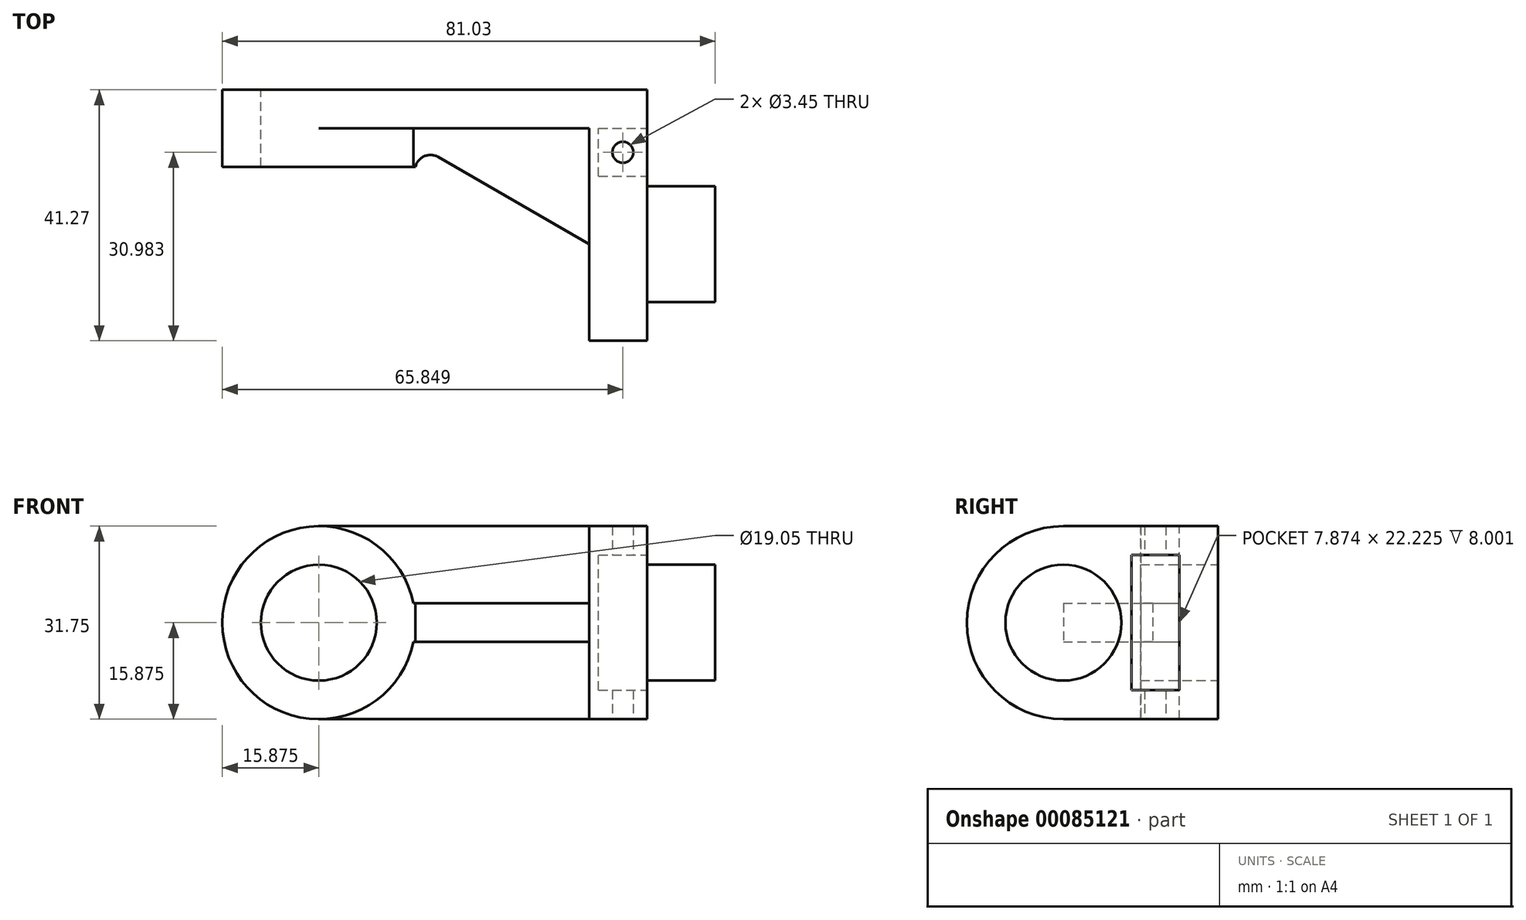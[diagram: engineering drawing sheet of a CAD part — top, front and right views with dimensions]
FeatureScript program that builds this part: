
annotation { "Feature Type Name" : "Feature", "Feature Type Description" : "" }
export const myFeature = defineFeature(function(context is Context, id is Id, definition is map)
    precondition{}
    {
        {
            var Q0;
            Q0=qCreatedBy(makeId("Front.planeOp"),FACE);
            var sketch = newSketch(context, id + "F0", { "sketchPlane" : qUnion([Q0])});
            skLineSegment(sketch, "E0.bottom", {"start": v(0, 0) * mm, "end": v(-53.98, 0) * mm});
            skLineSegment(sketch, "E0.top", {"start": v(0, 31.75) * mm, "end": v(-53.97, 31.75) * mm});
            skLineSegment(sketch, "E0.left", {"start": v(0, 0) * mm, "end": v(0, 31.75) * mm});
            skLineSegment(sketch, "E0.right", {"start": v(-53.98, 0) * mm, "end": v(-53.97, 31.75) * mm});
            skCircle(sketch, "E1", {"center": v(-53.97, 15.88) * mm, "radius": 15.88 * mm});
            skCircle(sketch, "E2", {"center": v(-53.97, 15.88) * mm, "radius": 9.53 * mm});
            skLineSegment(sketch, "E3", {"start": v(-53.97, 15.87) * mm, "end": v(-69.9, 31.8) * mm, "construction": true});
            skLineSegment(sketch, "E4", {"start": v(-69.9, 31.8) * mm, "end": v(-53.97, 15.87) * mm, "construction": true});
            skLineSegment(sketch, "E5", {"start": v(-53.97, 15.88) * mm, "end": v(-71.56, -1.7) * mm, "construction": true});
            skLineSegment(sketch, "E6", {"start": v(-24.5, 15.88) * mm, "end": v(-108.08, 15.88) * mm, "construction": true});
            skSolve(sketch);
        }
        {
            var Q0;
            {var subQ1=sQuery(id+"F0.wireOp",EDGE,"E0.right");var subQ3=sQuery(id+"F0.wireOp",EDGE,"E2");var subQ4=makeQuery(id+"F0.imprint","INTERSECT",VERTEX,{"disambiguationData":[OD(0.0)],"derivedFrom":[subQ1,subQ3]});Q0=makeQuery(id+"F0.imprint","IMPRINT",FACE,{"disambiguationData":[TD([[makeQuery(id+"F0.imprint","IMPRINT",EDGE,{"disambiguationData":[TD([[subQ4,1.0]])],"derivedFrom":subQ3}),-1.0]])]});}
            var Q1;
            {var subQ1=sQuery(id+"F0.wireOp",EDGE,"E0.right");var subQ3=sQuery(id+"F0.wireOp",EDGE,"E2");var subQ4=makeQuery(id+"F0.imprint","INTERSECT",VERTEX,{"disambiguationData":[OD(0.0)],"derivedFrom":[subQ1,subQ3]});Q1=makeQuery(id+"F0.imprint","IMPRINT",FACE,{"disambiguationData":[TD([[makeQuery(id+"F0.imprint","IMPRINT",EDGE,{"disambiguationData":[TD([[subQ4,-1.0]])],"derivedFrom":subQ3}),-1.0]])]});}
            extrude(context, id + "F1", {"entities" : qUnion([Q0, Q1]), "endBound" : BoundingType.SYMMETRIC, "depth" : 12.7 * mm});
        }
        {
            var Q0;
            {var subQ0=sQuery(id+"F0.wireOp",EDGE,"E0.bottom");Q0=makeQuery(id+"F0.imprint","IMPRINT",FACE,{"disambiguationData":[TD([[makeQuery(id+"F0.imprint","IMPRINT",EDGE,{"derivedFrom":subQ0}),-1.0]])]});}
            extrude(context, id + "F2", {"entities" : qUnion([Q0]), "operationType" : NewBodyOperationType.ADD, "oppositeDirection" : true, "depth" : 6.35 * mm});
        }
        {
            var Q0;
            Q0=sQuery(id+"F0.wireOp",EDGE,"E6");
            cPlane(context, id + "F3", {"entities" : qUnion([Q0]), "cplaneType" : CPlaneType.LINE_ANGLE, "offset" : 152.4 * mm, "angle" : 90 * degree, "width" : 152.4 * mm, "height" : 152.4 * mm});
        }
        {
            var Q0;
            Q0=makeQuery(id+"F2.opExtrude","SWEPT_FACE",FACE,{"disambiguationData":[OSD([sQuery(id+"F0.wireOp",EDGE,"E0.left")])]});
            var sketch = newSketch(context, id + "F4", { "sketchPlane" : qUnion([Q0])});
            skLineSegment(sketch, "E7.0", {"start": v(6.35, 0) * mm, "end": v(6.35, 31.75) * mm});
            skLineSegment(sketch, "E8.0", {"start": v(6.35, 0) * mm, "end": v(0, 0) * mm});
            skLineSegment(sketch, "E8.1", {"start": v(6.35, 31.75) * mm, "end": v(0, 31.75) * mm});
            skLineSegment(sketch, "E9.0", {"start": v(-6.35, 0) * mm, "end": v(-6.35, 31.75) * mm});
            skLineSegment(sketch, "E10", {"start": v(6.35, 15.88) * mm, "end": v(-51.97, 15.88) * mm, "construction": true});
            skCircle(sketch, "E11", {"center": v(-19.05, 15.88) * mm, "radius": 9.53 * mm});
            skLineSegment(sketch, "E12", {"start": v(-19.05, 31.75) * mm, "end": v(-19.05, 0) * mm, "construction": true});
            skArc(sketch, "E13", {"start": v(-19.05, 0) * mm, "mid": v(-34.93, 15.88) * mm, "end": v(-19.05, 31.75) * mm});
            skLineSegment(sketch, "E14", {"start": v(-19.05, 0) * mm, "end": v(-6.35, 0) * mm});
            skLineSegment(sketch, "E15", {"start": v(-19.05, 31.75) * mm, "end": v(-6.35, 31.75) * mm});
            skLineSegment(sketch, "E16", {"start": v(-6.35, 0) * mm, "end": v(0, 0) * mm});
            skLineSegment(sketch, "E17", {"start": v(-6.35, 31.75) * mm, "end": v(0, 31.75) * mm});
            skSolve(sketch);
        }
        {
            var Q0;
            Q0=makeQuery(id+"F4.imprint","IMPRINT",FACE,{"disambiguationData":[TD([[makeQuery(id+"F4.imprint","IMPRINT",EDGE,{"derivedFrom":sQuery(id+"F4.wireOp",EDGE,"E9.0")}),1.0]])]});
            var Q1;
            Q1=makeQuery(id+"F4.imprint","IMPRINT",FACE,{"disambiguationData":[TD([[makeQuery(id+"F4.imprint","IMPRINT",EDGE,{"derivedFrom":sQuery(id+"F4.wireOp",EDGE,"E9.0")}),-1.0]])]});
            var Q2;
            Q2=makeQuery(id+"F4.imprint","IMPRINT",FACE,{"disambiguationData":[TD([[makeQuery(id+"F4.imprint","IMPRINT",EDGE,{"derivedFrom":sQuery(id+"F4.wireOp",EDGE,"E11")}),1.0]])]});
            extrude(context, id + "F5", {"entities" : qUnion([Q0, Q1, Q2]), "operationType" : NewBodyOperationType.ADD, "oppositeDirection" : true, "depth" : 9.52 * mm});
        }
        {
            var Q0;
            Q0=makeQuery(id+"F4.imprint","IMPRINT",FACE,{"disambiguationData":[TD([[makeQuery(id+"F4.imprint","IMPRINT",EDGE,{"derivedFrom":sQuery(id+"F4.wireOp",EDGE,"E11")}),1.0]])]});
            extrude(context, id + "F6", {"entities" : qUnion([Q0]), "operationType" : NewBodyOperationType.ADD, "depth" : 11.18 * mm});
        }
        {
            var Q0;
            Q0=qCreatedBy(id+"F3.planeOp",FACE);
            var sketch = newSketch(context, id + "F7", { "sketchPlane" : qUnion([Q0])});
            skLineSegment(sketch, "E18.0", {"start": v(-9.53, -19.05) * mm, "end": v(-9.53, 0) * mm});
            skLineSegment(sketch, "E18.1", {"start": v(-9.53, -34.93) * mm, "end": v(-9.53, -19.05) * mm});
            skLineSegment(sketch, "E18.2", {"start": v(0, 0) * mm, "end": v(-53.97, 0) * mm});
            skLineSegment(sketch, "E18.3", {"start": v(-38.1, -6.35) * mm, "end": v(-69.85, -6.35) * mm});
            skLineSegment(sketch, "E18.4", {"start": v(-53.97, 6.35) * mm, "end": v(-53.97, 0) * mm});
            skLineSegment(sketch, "E19", {"start": v(-9.52, -19.05) * mm, "end": v(-34.35, -4.72) * mm});
            skArc(sketch, "E20", {"start": v(-34.35, -4.72) * mm, "mid": v(-36.64, -4.59) * mm, "end": v(-38.1, -6.35) * mm});
            skLineSegment(sketch, "E21.0", {"start": v(-38.1, 0) * mm, "end": v(-69.85, 0) * mm});
            skLineSegment(sketch, "E21.1", {"start": v(-44.45, -6.35) * mm, "end": v(-63.5, -6.35) * mm});
            skLineSegment(sketch, "E22", {"start": v(-44.45, -6.35) * mm, "end": v(-44.45, 0) * mm});
            skSolve(sketch);
        }
        {
            var Q0;
            {var subQ2=sQuery(id+"F7.wireOp",EDGE,"E18.0");Q0=makeQuery(id+"F7.imprint","IMPRINT",FACE,{"disambiguationData":[TD([[makeQuery(id+"F7.imprint","IMPRINT",EDGE,{"derivedFrom":subQ2}),1.0]])]});}
            extrude(context, id + "F8", {"entities" : qUnion([Q0]), "operationType" : NewBodyOperationType.ADD, "endBound" : BoundingType.SYMMETRIC, "depth" : 6.35 * mm});
        }
        {
            var Q0;
            Q0=makeQuery(id+"F4.imprint","IMPRINT",FACE,{"disambiguationData":[TD([[makeQuery(id+"F4.imprint","IMPRINT",EDGE,{"derivedFrom":sQuery(id+"F4.wireOp",EDGE,"E9.0")}),-1.0]])]});
            var sketch = newSketch(context, id + "F9", { "sketchPlane" : qUnion([Q0])});
            skLineSegment(sketch, "E23.0", {"start": v(-6.35, 0) * mm, "end": v(0, 0) * mm});
            skLineSegment(sketch, "E23.1", {"start": v(-19.05, 0) * mm, "end": v(-6.35, 0) * mm});
            skLineSegment(sketch, "E23.2", {"start": v(-19.05, 31.75) * mm, "end": v(-6.35, 31.75) * mm});
            skLineSegment(sketch, "E23.3", {"start": v(-6.35, 31.75) * mm, "end": v(0, 31.75) * mm});
            skLineSegment(sketch, "E23.4", {"start": v(6.35, 0) * mm, "end": v(6.35, 31.75) * mm});
            skLineSegment(sketch, "E23.5", {"start": v(6.35, 0) * mm, "end": v(0, 0) * mm});
            skLineSegment(sketch, "E23.6", {"start": v(6.35, 31.75) * mm, "end": v(0, 31.75) * mm});
            skArc(sketch, "E23.7", {"start": v(-19.05, 0) * mm, "mid": v(-34.93, 15.88) * mm, "end": v(-19.05, 31.75) * mm});
            skLineSegment(sketch, "E24.bottom", {"start": v(-7.87, 4.78) * mm, "end": v(0, 4.78) * mm});
            skLineSegment(sketch, "E24.top", {"start": v(-7.87, 27) * mm, "end": v(0, 27) * mm});
            skLineSegment(sketch, "E24.left", {"start": v(-7.87, 4.78) * mm, "end": v(-7.87, 27) * mm});
            skLineSegment(sketch, "E24.right", {"start": v(0, 4.78) * mm, "end": v(0, 27) * mm});
            skSolve(sketch);
        }
        {
            var Q0;
            Q0=makeQuery(id+"F9.imprint","IMPRINT",FACE,{"disambiguationData":[TD([[makeQuery(id+"F9.imprint","IMPRINT",EDGE,{"derivedFrom":sQuery(id+"F9.wireOp",EDGE,"E24.bottom")}),1.0]])]});
            extrude(context, id + "F10", {"entities" : qUnion([Q0]), "operationType" : NewBodyOperationType.REMOVE, "oppositeDirection" : true, "depth" : 8 * mm});
        }
        {
            var Q0;
            Q0=makeQuery(id+"F5.boolean.opBoolean","MERGE",FACE,{"derivedFrom":[makeQuery(id+"F2.opExtrude","SWEPT_FACE",FACE,{"disambiguationData":[OSD([sQuery(id+"F0.wireOp",EDGE,"E0.bottom")])]}),makeQuery(id+"F5.opExtrude","SWEPT_FACE",FACE,{"disambiguationData":[OSD([sQuery(id+"F4.wireOp",EDGE,"E14"),sQuery(id+"F4.wireOp",EDGE,"E16")])]})]});
            var sketch = newSketch(context, id + "F11", { "sketchPlane" : qUnion([Q0])});
            skLineSegment(sketch, "E25.0", {"start": v(-8, 7.87) * mm, "end": v(-8, 0) * mm});
            skLineSegment(sketch, "E25.1", {"start": v(0, 7.87) * mm, "end": v(0, 0) * mm});
            skLineSegment(sketch, "E25.3", {"start": v(-8, 7.87) * mm, "end": v(0, 7.87) * mm});
            skLineSegment(sketch, "E25.4", {"start": v(-8, 0) * mm, "end": v(0, 0) * mm});
            skLineSegment(sketch, "E26", {"start": v(0, 7.87) * mm, "end": v(-8, 0) * mm, "construction": true});
            skCircle(sketch, "E27", {"center": v(-4, 3.94) * mm, "radius": 1.73 * mm});
            skSolve(sketch);
        }
        {
            var Q0;
            Q0=makeQuery(id+"F11.imprint","IMPRINT",FACE,{"disambiguationData":[TD([[makeQuery(id+"F11.imprint","IMPRINT",EDGE,{"derivedFrom":sQuery(id+"F11.wireOp",EDGE,"E27")}),1.0]])]});
            extrude(context, id + "F12", {"entities" : qUnion([Q0]), "operationType" : NewBodyOperationType.REMOVE, "endBound" : BoundingType.THROUGH_ALL, "oppositeDirection" : true, "depth" : 25.4 * mm});
        }
    });
